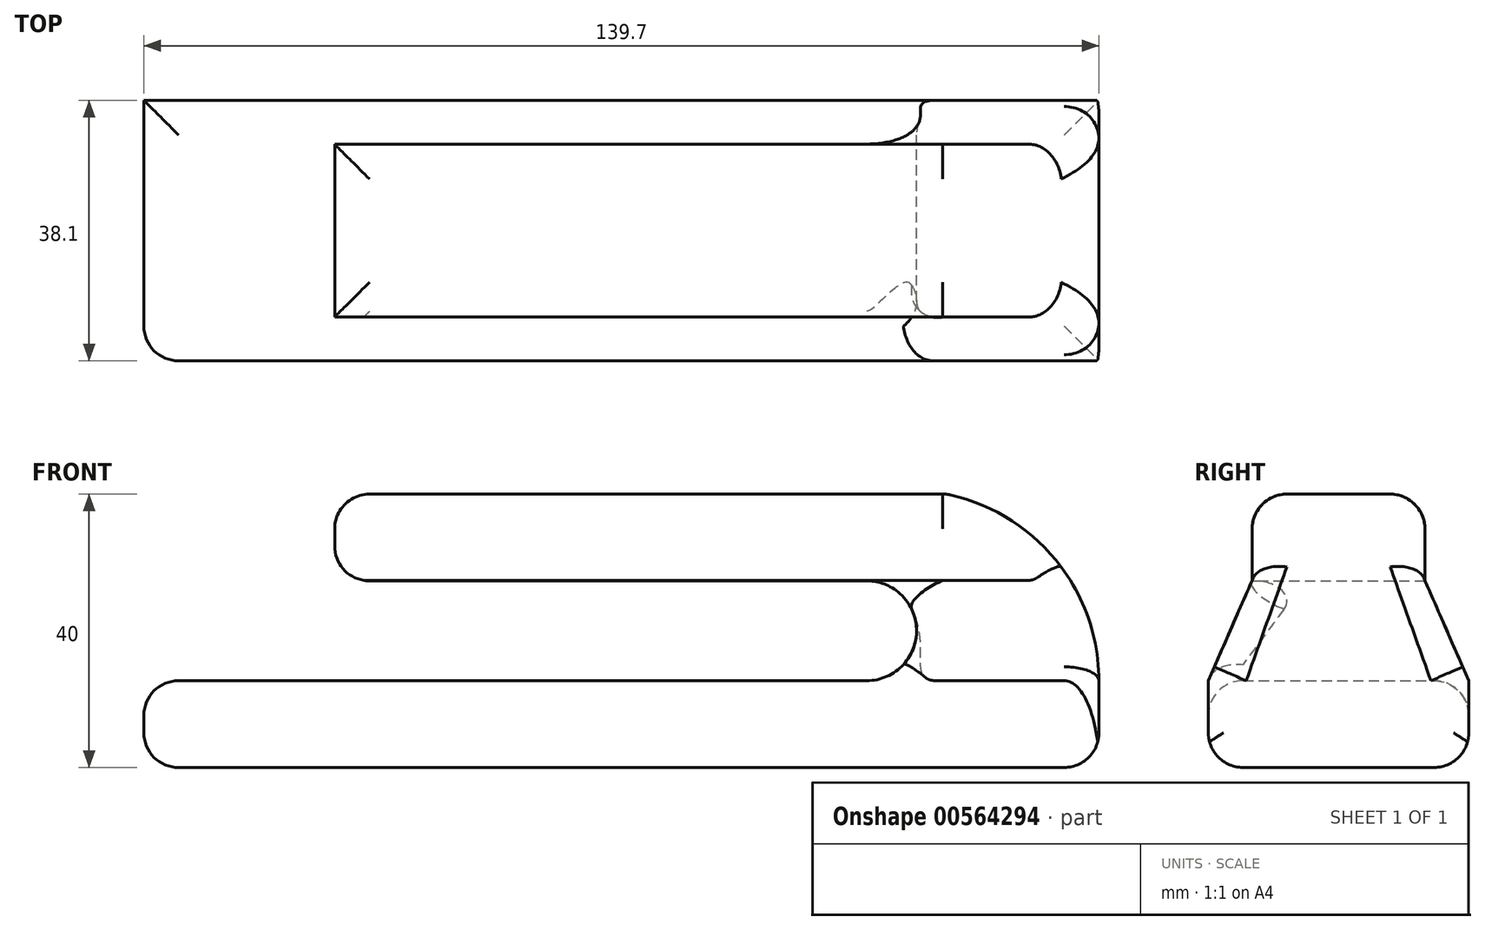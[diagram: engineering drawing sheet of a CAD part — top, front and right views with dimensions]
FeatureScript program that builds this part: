
annotation { "Feature Type Name" : "Feature", "Feature Type Description" : "" }
export const myFeature = defineFeature(function(context is Context, id is Id, definition is map)
    precondition{}
    {
        {
            var Q0;
            Q0=qCreatedBy(makeId("Front.planeOp"),FACE);
            var sketch = newSketch(context, id + "F0", { "sketchPlane" : qUnion([Q0])});
            skLineSegment(sketch, "E0.bottom", {"start": v(67.16, 0) * mm, "end": v(-72.54, 0) * mm});
            skLineSegment(sketch, "E0.left", {"start": v(67.16, 0) * mm, "end": v(67.16, 12.7) * mm});
            skLineSegment(sketch, "E0.right", {"start": v(-72.54, 0) * mm, "end": v(-72.54, 12.7) * mm});
            skLineSegment(sketch, "E1", {"start": v(-44.62, 27.3) * mm, "end": v(-44.62, 40) * mm});
            skLineSegment(sketch, "E2", {"start": v(-44.62, 40) * mm, "end": v(44.84, 40) * mm});
            skArc(sketch, "E3", {"start": v(67.16, 12.7) * mm, "mid": v(60.87, 30.33) * mm, "end": v(44.84, 40) * mm});
            skLineSegment(sketch, "E4", {"start": v(73.54, 0) * mm, "end": v(73.54, 49.57) * mm});
            skLineSegment(sketch, "E5", {"start": v(-44.62, 27.3) * mm, "end": v(33.18, 27.3) * mm});
            skArc(sketch, "E6", {"start": v(33.18, 12.7) * mm, "mid": v(40.48, 20) * mm, "end": v(33.18, 27.3) * mm});
            skLineSegment(sketch, "E7", {"start": v(-72.54, 12.7) * mm, "end": v(33.18, 12.7) * mm});
            skSolve(sketch);
        }
        {
            var Q0;
            Q0 = qSketchRegion(id + "F0", true);
            extrude(context, id + "F1", {"entities" : qUnion([Q0]), "depth" : 38.1 * mm, "offsetDistance" : 25.4 * mm});
        }
        {
            var Q0;
            Q0=qCreatedBy(makeId("Right.planeOp"),FACE);
            var sketch = newSketch(context, id + "F2", { "sketchPlane" : qUnion([Q0])});
            skLineSegment(sketch, "E8", {"start": v(0, 12.7) * mm, "end": v(0, 40.1) * mm});
            skLineSegment(sketch, "E9", {"start": v(0, 12.7) * mm, "end": v(-6.42, 27.37) * mm});
            skLineSegment(sketch, "E10", {"start": v(-31.69, 27.37) * mm, "end": v(-38.1, 12.7) * mm});
            skLineSegment(sketch, "E11", {"start": v(-31.69, 27.37) * mm, "end": v(-31.69, 45.15) * mm});
            skLineSegment(sketch, "E12", {"start": v(-31.69, 45.15) * mm, "end": v(-38.1, 45.15) * mm});
            skLineSegment(sketch, "E13", {"start": v(-38.1, 45.15) * mm, "end": v(-38.1, 12.7) * mm});
            skLineSegment(sketch, "E14", {"start": v(-6.42, 27.37) * mm, "end": v(-6.42, 45.15) * mm});
            skLineSegment(sketch, "E15", {"start": v(0, 12.7) * mm, "end": v(0, 45.15) * mm});
            skLineSegment(sketch, "E16", {"start": v(0, 45.15) * mm, "end": v(-6.42, 45.15) * mm});
            skSolve(sketch);
        }
        {
            var Q0;
            Q0 = qSketchRegion(id + "F2", true);
            extrude(context, id + "F3", {"entities" : qUnion([Q0]), "operationType" : NewBodyOperationType.REMOVE, "oppositeDirection" : true, "depth" : 228.6 * mm, "offsetDistance" : 25.4 * mm});
        }
        {
            var Q0;
            Q0 = qSketchRegion(id + "F2", true);
            extrude(context, id + "F4", {"entities" : qUnion([Q0]), "operationType" : NewBodyOperationType.REMOVE, "oppositeDirection" : true, "depth" : -228.6 * mm, "offsetDistance" : 25.4 * mm});
        }
        {
            var Q0;
            Q0=makeQuery(id+"F1.opExtrude","CAP_EDGE",EDGE,{"disambiguationData":[OSD([sQuery(id+"F0.wireOp",EDGE,"E7")])],"isStart":true});
            var Q1;
            Q1=makeQuery(id+"F4.boolean.opBoolean","INTERSECT",EDGE,{"derivedFrom":[makeQuery(id+"F1.opExtrude","SWEPT_FACE",FACE,{"disambiguationData":[OSD([sQuery(id+"F0.wireOp",EDGE,"E2")])]}),makeQuery(id+"F4.opExtrude","SWEPT_FACE",FACE,{"disambiguationData":[OSD([sQuery(id+"F2.wireOp",EDGE,"E11")])]})]});
            var Q2;
            Q2=makeQuery(id+"F4.boolean.opBoolean","INTERSECT",EDGE,{"derivedFrom":[makeQuery(id+"F1.opExtrude","SWEPT_FACE",FACE,{"disambiguationData":[OSD([sQuery(id+"F0.wireOp",EDGE,"E2")])]}),makeQuery(id+"F4.opExtrude","SWEPT_FACE",FACE,{"disambiguationData":[OSD([sQuery(id+"F2.wireOp",EDGE,"E14")])]})]});
            var Q3;
            Q3=makeQuery(id+"F1.opExtrude","SWEPT_EDGE",EDGE,{"disambiguationData":[OSD([sQuery(id+"F0.wireOp",EDGE,"E1"),sQuery(id+"F0.wireOp",EDGE,"E2")])]});
            var Q4;
            Q4=makeQuery(id+"F1.opExtrude","SWEPT_EDGE",EDGE,{"disambiguationData":[OSD([sQuery(id+"F0.wireOp",EDGE,"E1"),sQuery(id+"F0.wireOp",EDGE,"E5")])]});
            var Q5;
            Q5=makeQuery(id+"F4.boolean.opBoolean","INTERSECT",EDGE,{"derivedFrom":[makeQuery(id+"F1.opExtrude","SWEPT_FACE",FACE,{"disambiguationData":[OSD([sQuery(id+"F0.wireOp",EDGE,"E5")])]}),makeQuery(id+"F4.opExtrude","SWEPT_FACE",FACE,{"disambiguationData":[OSD([sQuery(id+"F2.wireOp",EDGE,"E10")])]})]});
            var Q6;
            Q6=makeQuery(id+"F1.opExtrude","SWEPT_EDGE",EDGE,{"disambiguationData":[OSD([sQuery(id+"F0.wireOp",EDGE,"E0.right"),sQuery(id+"F0.wireOp",EDGE,"E7")])]});
            var Q7;
            Q7=makeQuery(id+"F1.opExtrude","CAP_EDGE",EDGE,{"disambiguationData":[OSD([sQuery(id+"F0.wireOp",EDGE,"E0.bottom")])],"isStart":true});
            var Q8;
            Q8=makeQuery(id+"F1.opExtrude","SWEPT_EDGE",EDGE,{"disambiguationData":[OSD([sQuery(id+"F0.wireOp",EDGE,"E0.bottom"),sQuery(id+"F0.wireOp",EDGE,"E0.right")])]});
            var Q9;
            Q9=makeQuery(id+"F1.opExtrude","SWEPT_EDGE",EDGE,{"disambiguationData":[OSD([sQuery(id+"F0.wireOp",EDGE,"E0.bottom"),sQuery(id+"F0.wireOp",EDGE,"E0.left")])]});
            var Q10;
            Q10=makeQuery(id+"F1.opExtrude","CAP_EDGE",EDGE,{"disambiguationData":[OSD([sQuery(id+"F0.wireOp",EDGE,"E0.bottom")])],"isStart":false});
            fillet(context, id + "F5", {"entities" : qUnion([Q0, Q1, Q2, Q3, Q4, Q5, Q6, Q7, Q8, Q9, Q10]), "radius" : 5.08 * mm, "tangentPropagation" : true, "allowEdgeOverflow" : false});
        }
        {
            var Q0;
            {var subQ0=sQuery(id+"F0.wireOp",EDGE,"E7");var subQ1=sQuery(id+"F0.wireOp",EDGE,"E6");Q0=makeQuery(id+"F4.boolean.opBoolean","SPLIT",EDGE,{"disambiguationData":[TD([makeQuery(id+"F1.opExtrude","SWEPT_FACE",FACE,{"disambiguationData":[OSD([subQ1])]})])],"derivedFrom":makeQuery(id+"F1.opExtrude","CAP_EDGE",EDGE,{"disambiguationData":[OSD([subQ0])],"isStart":false})});}
            var Q1;
            {var subQ0=sQuery(id+"F0.wireOp",EDGE,"E7");var subQ1=sQuery(id+"F0.wireOp",EDGE,"E0.right");Q1=makeQuery(id+"F4.boolean.opBoolean","SPLIT",EDGE,{"disambiguationData":[TD([makeQuery(id+"F1.opExtrude","SWEPT_FACE",FACE,{"disambiguationData":[OSD([subQ1])]})])],"derivedFrom":makeQuery(id+"F1.opExtrude","CAP_EDGE",EDGE,{"disambiguationData":[OSD([subQ0])],"isStart":false})});}
            var Q2;
            Q2=makeQuery(id+"F4.boolean.opBoolean","INTERSECT",EDGE,{"derivedFrom":[makeQuery(id+"F1.opExtrude","SWEPT_FACE",FACE,{"disambiguationData":[OSD([sQuery(id+"F0.wireOp",EDGE,"E3")])]}),makeQuery(id+"F4.opExtrude","SWEPT_FACE",FACE,{"disambiguationData":[OSD([sQuery(id+"F2.wireOp",EDGE,"E10")])]})]});
            var Q3;
            Q3=makeQuery(id+"F4.boolean.opBoolean","INTERSECT",EDGE,{"derivedFrom":[makeQuery(id+"F1.opExtrude","SWEPT_FACE",FACE,{"disambiguationData":[OSD([sQuery(id+"F0.wireOp",EDGE,"E3")])]}),makeQuery(id+"F4.opExtrude","SWEPT_FACE",FACE,{"disambiguationData":[OSD([sQuery(id+"F2.wireOp",EDGE,"E11")])]})]});
            var Q4;
            Q4=makeQuery(id+"F4.boolean.opBoolean","INTERSECT",EDGE,{"derivedFrom":[makeQuery(id+"F1.opExtrude","SWEPT_FACE",FACE,{"disambiguationData":[OSD([sQuery(id+"F0.wireOp",EDGE,"E3")])]}),makeQuery(id+"F4.opExtrude","SWEPT_FACE",FACE,{"disambiguationData":[OSD([sQuery(id+"F2.wireOp",EDGE,"E9")])]})]});
            fillet(context, id + "F6", {"entities" : qUnion([Q0, Q1, Q2, Q3, Q4]), "radius" : 5.08 * mm, "tangentPropagation" : true, "allowEdgeOverflow" : false});
        }
    });
